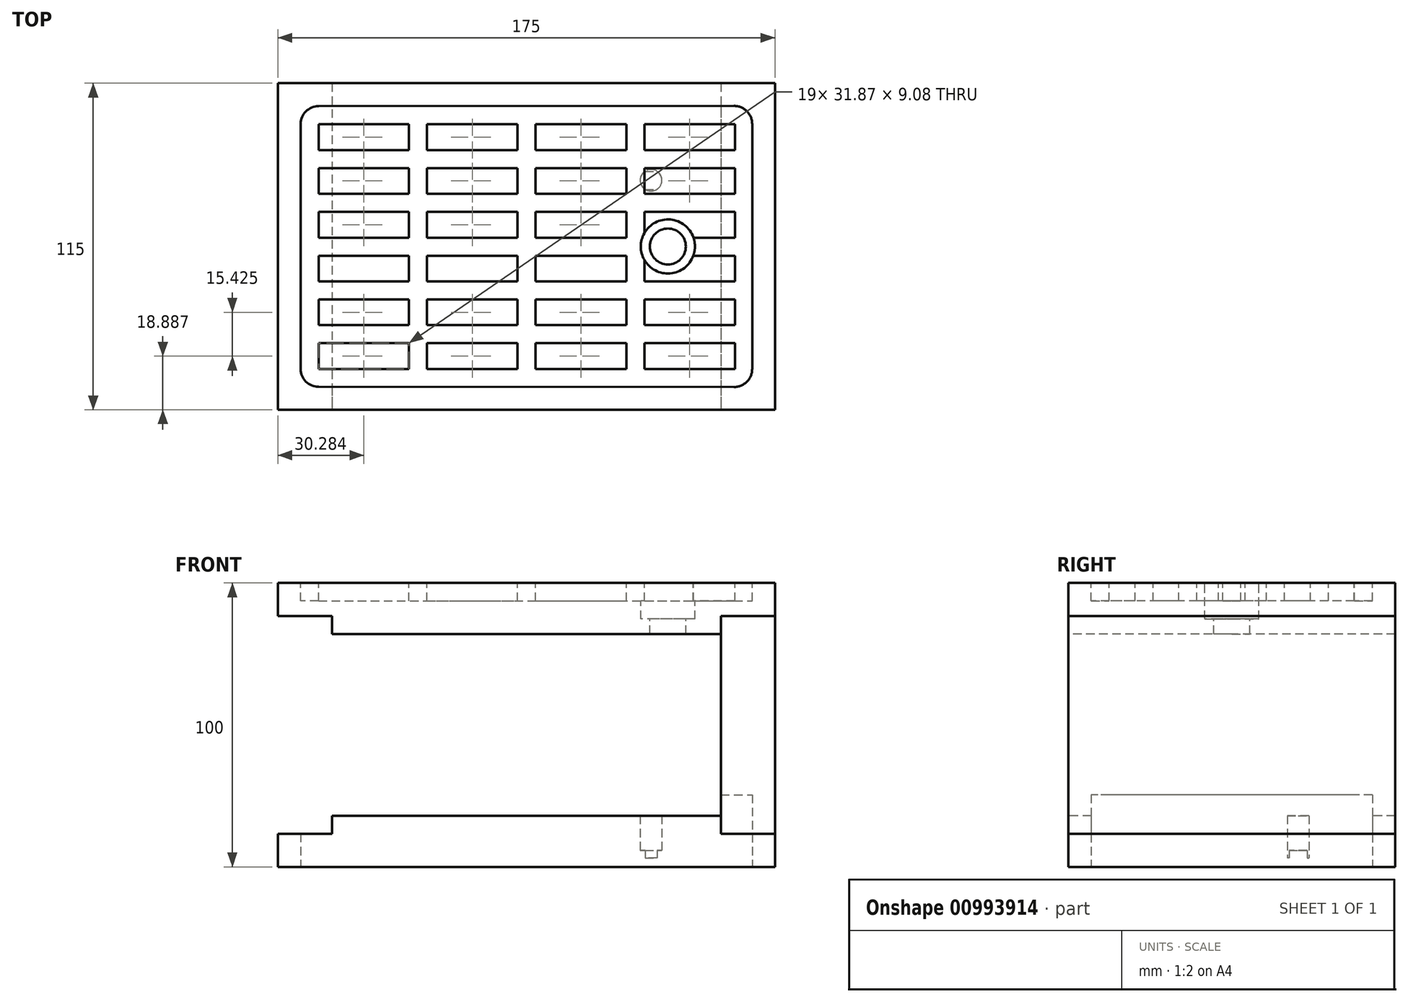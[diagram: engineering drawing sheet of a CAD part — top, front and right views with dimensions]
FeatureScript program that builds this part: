
annotation { "Feature Type Name" : "Feature", "Feature Type Description" : "" }
export const myFeature = defineFeature(function(context is Context, id is Id, definition is map)
    precondition{}
    {
        {
            var Q0;
            Q0=qCreatedBy(makeId("Front.planeOp"),FACE);
            var sketch = newSketch(context, id + "F0", { "sketchPlane" : qUnion([Q0])});
            skLineSegment(sketch, "E0.bottom", {"start": v(-125.12, 38.1) * mm, "end": v(49.88, 38.1) * mm});
            skLineSegment(sketch, "E0.top", {"start": v(-106.07, 20.1) * mm, "end": v(30.83, 20.1) * mm});
            skLineSegment(sketch, "E0.left", {"start": v(-125.12, 38.1) * mm, "end": v(-125.12, 26.44) * mm});
            skLineSegment(sketch, "E0.right", {"start": v(49.88, 38.1) * mm, "end": v(49.88, 26.44) * mm});
            skLineSegment(sketch, "E1", {"start": v(-37.62, 50.38) * mm, "end": v(-37.62, -79.55) * mm, "construction": true});
            skPoint(sketch, "E1.startSnap0", {"position": v(-37.62, 38.1) * mm});
            skLineSegment(sketch, "E2.bottom", {"start": v(-106.07, 26.44) * mm, "end": v(-125.12, 26.44) * mm});
            skLineSegment(sketch, "E2.left", {"start": v(-106.07, 26.44) * mm, "end": v(-106.07, 20.1) * mm});
            skLineSegment(sketch, "E3.MirrorCS", {"start": v(30.83, 26.44) * mm, "end": v(49.88, 26.44) * mm});
            skLineSegment(sketch, "E4.MirrorCS", {"start": v(30.83, 20.1) * mm, "end": v(30.83, 26.44) * mm});
            skLineSegment(sketch, "E5", {"start": v(-152.81, -11.9) * mm, "end": v(116.81, -11.9) * mm, "construction": true});
            skLineSegment(sketch, "E6.MirrorCS", {"start": v(-125.12, -61.9) * mm, "end": v(49.88, -61.9) * mm});
            skLineSegment(sketch, "E7.MirrorCS", {"start": v(-106.07, -43.9) * mm, "end": v(30.83, -43.9) * mm});
            skLineSegment(sketch, "E8.MirrorCS", {"start": v(-106.07, -50.26) * mm, "end": v(-125.12, -50.26) * mm});
            skLineSegment(sketch, "E9.MirrorCS", {"start": v(-106.07, -43.9) * mm, "end": v(-106.07, -50.26) * mm});
            skLineSegment(sketch, "E10.MirrorCS", {"start": v(30.83, -43.9) * mm, "end": v(30.83, -50.26) * mm});
            skLineSegment(sketch, "E11.MirrorCS", {"start": v(30.83, -50.26) * mm, "end": v(49.88, -50.26) * mm});
            skLineSegment(sketch, "E12.MirrorCS", {"start": v(49.88, -61.9) * mm, "end": v(49.88, -50.26) * mm});
            skLineSegment(sketch, "E13", {"start": v(-125.12, -50.26) * mm, "end": v(-125.12, -61.9) * mm});
            skLineSegment(sketch, "E14.left", {"start": v(-106.07, 26.44) * mm, "end": v(-106.07, -50.26) * mm, "construction": true});
            skLineSegment(sketch, "E14.right", {"start": v(-125.12, 26.44) * mm, "end": v(-125.12, -50.26) * mm, "construction": true});
            skLineSegment(sketch, "E15.MirrorCS", {"start": v(49.88, 26.44) * mm, "end": v(49.88, -50.26) * mm, "construction": true});
            skLineSegment(sketch, "E16.MirrorCS", {"start": v(30.83, 26.44) * mm, "end": v(30.83, -50.26) * mm, "construction": true});
            skLineSegment(sketch, "E17.left", {"start": v(30.83, 26.44) * mm, "end": v(30.83, -50.26) * mm});
            skLineSegment(sketch, "E17.right", {"start": v(49.88, 26.44) * mm, "end": v(49.88, -50.26) * mm});
            skSolve(sketch);
        }
        {
            var Q0;
            Q0=makeQuery(id+"F0.imprint","IMPRINT",FACE,{"disambiguationData":[TD([[makeQuery(id+"F0.imprint","IMPRINT",EDGE,{"derivedFrom":sQuery(id+"F0.wireOp",EDGE,"E0.bottom")}),-1.0]])]});
            var Q1;
            Q1=makeQuery(id+"F0.imprint","IMPRINT",FACE,{"disambiguationData":[TD([[makeQuery(id+"F0.imprint","IMPRINT",EDGE,{"derivedFrom":sQuery(id+"F0.wireOp",EDGE,"E6.MirrorCS")}),1.0]])]});
            extrude(context, id + "F1", {"entities" : qUnion([Q0, Q1]), "oppositeDirection" : true, "depth" : 115 * mm, "offsetDistance" : 25.4 * mm});
        }
        {
            var Q0;
            Q0 = qSketchRegion(id + "F0", true);
            extrude(context, id + "F2", {"entities" : qUnion([Q0]), "oppositeDirection" : true, "depth" : 115 * mm, "offsetDistance" : 25.4 * mm});
        }
        {
            var Q0;
            Q0=makeQuery(id+"F1.opExtrude","SWEPT_FACE",FACE,{"disambiguationData":[OSD([sQuery(id+"F0.wireOp",EDGE,"E0.bottom")])]});
            var sketch = newSketch(context, id + "F3", { "sketchPlane" : qUnion([Q0])});
            skLineSegment(sketch, "E18", {"start": v(64.2, 57.5) * mm, "end": v(21.17, 57.5) * mm, "construction": true});
            skPoint(sketch, "E18.startSnap0", {"position": v(49.88, 57.5) * mm});
            skPoint(sketch, "E19.startSnap0", {"position": v(-37.62, 115) * mm});
            skLineSegment(sketch, "E20.0", {"start": v(-110.77, 100.55) * mm, "end": v(-78.9, 100.55) * mm});
            skLineSegment(sketch, "E21.0", {"start": v(-110.77, 100.55) * mm, "end": v(-110.77, 91.47) * mm});
            skLineSegment(sketch, "E22.trimOffspring", {"start": v(-110.77, 14.35) * mm, "end": v(-78.9, 14.35) * mm});
            skArc(sketch, "E23", {"start": v(-110.78, 106.9) * mm, "mid": v(-115.23, 105.07) * mm, "end": v(-117.12, 100.65) * mm});
            skArc(sketch, "E24.MirrorCS", {"start": v(35.52, 107) * mm, "mid": v(40.02, 105.14) * mm, "end": v(41.88, 100.65) * mm});
            skArc(sketch, "E25.MirrorCS", {"start": v(-110.78, 8.1) * mm, "mid": v(-115.23, 9.93) * mm, "end": v(-117.12, 14.35) * mm});
            skArc(sketch, "E26.MirrorCS", {"start": v(35.52, 8) * mm, "mid": v(40.02, 9.86) * mm, "end": v(41.88, 14.35) * mm});
            skLineSegment(sketch, "E27.0", {"start": v(-110.77, 91.47) * mm, "end": v(-78.9, 91.47) * mm});
            skLineSegment(sketch, "E28.0", {"start": v(-110.77, 85.12) * mm, "end": v(-78.9, 85.12) * mm});
            skLineSegment(sketch, "E29.0", {"start": v(-110.77, 76.05) * mm, "end": v(-78.9, 76.05) * mm});
            skLineSegment(sketch, "E30.0", {"start": v(-110.77, 69.7) * mm, "end": v(-78.9, 69.7) * mm});
            skLineSegment(sketch, "E31.0", {"start": v(-110.77, 60.63) * mm, "end": v(-78.9, 60.63) * mm});
            skLineSegment(sketch, "E32.0", {"start": v(-110.77, 54.28) * mm, "end": v(3.25, 54.28) * mm});
            skLineSegment(sketch, "E33.0", {"start": v(-110.77, 45.2) * mm, "end": v(-78.9, 45.2) * mm});
            skLineSegment(sketch, "E34.0", {"start": v(-110.77, 38.85) * mm, "end": v(-78.9, 38.85) * mm});
            skLineSegment(sketch, "E35.0", {"start": v(-110.77, 29.78) * mm, "end": v(-78.9, 29.78) * mm});
            skLineSegment(sketch, "E36.0", {"start": v(-110.77, 23.43) * mm, "end": v(-78.9, 23.43) * mm});
            skLineSegment(sketch, "E37.trimOffspring", {"start": v(-110.77, 85.12) * mm, "end": v(-110.77, 76.05) * mm});
            skLineSegment(sketch, "E38.trimOffspring", {"start": v(-110.77, 69.7) * mm, "end": v(-110.77, 60.63) * mm});
            skLineSegment(sketch, "E39.trimOffspring", {"start": v(-110.77, 54.28) * mm, "end": v(-110.77, 45.2) * mm});
            skLineSegment(sketch, "E40.trimOffspring", {"start": v(-110.77, 38.85) * mm, "end": v(-110.77, 29.78) * mm});
            skLineSegment(sketch, "E41.trimOffspring", {"start": v(-110.77, 23.43) * mm, "end": v(-110.77, 14.35) * mm});
            skLineSegment(sketch, "E42.0", {"start": v(-78.9, 100.55) * mm, "end": v(-78.9, 91.47) * mm});
            skLineSegment(sketch, "E43.0", {"start": v(-131.47, -6.35) * mm, "end": v(56.23, -6.35) * mm});
            skLineSegment(sketch, "E43.1", {"start": v(-131.47, 121.35) * mm, "end": v(-131.47, -6.35) * mm});
            skLineSegment(sketch, "E43.2", {"start": v(56.23, 121.35) * mm, "end": v(-131.47, 121.35) * mm});
            skLineSegment(sketch, "E43.3", {"start": v(56.23, -6.35) * mm, "end": v(56.23, 121.35) * mm});
            skLineSegment(sketch, "E44.trimOffspring", {"start": v(-78.9, 57.5) * mm, "end": v(-137, 57.5) * mm, "construction": true});
            skLineSegment(sketch, "E45.trimOffspring", {"start": v(-78.9, 23.43) * mm, "end": v(-78.9, 14.35) * mm});
            skLineSegment(sketch, "E46.trimOffspring", {"start": v(-78.9, 38.85) * mm, "end": v(-78.9, 29.78) * mm});
            skLineSegment(sketch, "E47.trimOffspring", {"start": v(-78.9, 54.28) * mm, "end": v(-78.9, 45.2) * mm});
            skLineSegment(sketch, "E48.trimOffspring", {"start": v(-78.9, 69.7) * mm, "end": v(-78.9, 60.63) * mm});
            skLineSegment(sketch, "E49.trimOffspring", {"start": v(-78.9, 85.12) * mm, "end": v(-78.9, 76.05) * mm});
            skLineSegment(sketch, "E50.MirrorCS", {"start": v(41.88, 100.65) * mm, "end": v(41.88, 14.25) * mm});
            skArc(sketch, "E51.MirrorCS", {"start": v(35.52, 8) * mm, "mid": v(39.98, 9.82) * mm, "end": v(41.88, 14.25) * mm});
            skLineSegment(sketch, "E52.bottom", {"start": v(-110.77, 54.28) * mm, "end": v(-78.9, 54.28) * mm});
            skCircle(sketch, "E53", {"center": v(12.2, 57.5) * mm, "radius": 6.32 * mm});
            skLineSegment(sketch, "E54", {"start": v(-94.84, 100.55) * mm, "end": v(-94.84, 91.47) * mm, "construction": true});
            skLineSegment(sketch, "E55", {"start": v(-94.84, 91.47) * mm, "end": v(-94.5, 90.59) * mm, "construction": true});
            skLineSegment(sketch, "E56", {"start": v(-94.84, 85.12) * mm, "end": v(-94.84, 76.05) * mm, "construction": true});
            skLineSegment(sketch, "E57", {"start": v(-94.84, 76.05) * mm, "end": v(-94.14, 76.72) * mm, "construction": true});
            skLineSegment(sketch, "E58", {"start": v(-94.84, 69.7) * mm, "end": v(-94.84, 60.63) * mm, "construction": true});
            skLineSegment(sketch, "E59", {"start": v(-94.84, 60.63) * mm, "end": v(-94.12, 61.09) * mm, "construction": true});
            skLineSegment(sketch, "E60", {"start": v(-94.84, 54.28) * mm, "end": v(-94.84, 45.2) * mm, "construction": true});
            skLineSegment(sketch, "E61", {"start": v(-94.84, 38.85) * mm, "end": v(-94.84, 29.78) * mm, "construction": true});
            skLineSegment(sketch, "E62", {"start": v(-94.84, 29.78) * mm, "end": v(-94.77, 30.91) * mm, "construction": true});
            skLineSegment(sketch, "E63", {"start": v(-94.84, 23.43) * mm, "end": v(-94.84, 14.35) * mm, "construction": true});
            skLineSegment(sketch, "E64", {"start": v(-94.84, 14.35) * mm, "end": v(-95.42, 15.1) * mm, "construction": true});
            skLineSegment(sketch, "E65.1.0.0", {"start": v(-40.67, 23.43) * mm, "end": v(-40.67, 14.35) * mm});
            skLineSegment(sketch, "E65.1.0.1", {"start": v(-40.67, 69.7) * mm, "end": v(-40.67, 60.63) * mm});
            skLineSegment(sketch, "E65.1.0.2", {"start": v(-72.54, 60.63) * mm, "end": v(-40.67, 60.63) * mm});
            skLineSegment(sketch, "E65.1.0.3", {"start": v(-40.67, 54.28) * mm, "end": v(-40.67, 45.2) * mm});
            skLineSegment(sketch, "E65.1.0.4", {"start": v(-72.54, 29.78) * mm, "end": v(-40.67, 29.78) * mm});
            skLineSegment(sketch, "E65.1.0.5", {"start": v(-72.54, 76.05) * mm, "end": v(-40.67, 76.05) * mm});
            skLineSegment(sketch, "E65.1.0.6", {"start": v(-56.6, 100.55) * mm, "end": v(-56.6, 91.47) * mm, "construction": true});
            skLineSegment(sketch, "E65.1.0.7", {"start": v(-56.6, 85.12) * mm, "end": v(-56.6, 76.05) * mm, "construction": true});
            skLineSegment(sketch, "E65.1.0.9", {"start": v(-72.54, 23.43) * mm, "end": v(-72.54, 14.35) * mm});
            skLineSegment(sketch, "E65.1.0.10", {"start": v(-72.54, 69.7) * mm, "end": v(-72.54, 60.63) * mm});
            skLineSegment(sketch, "E65.1.0.11", {"start": v(-40.67, 85.12) * mm, "end": v(-40.67, 76.05) * mm});
            skLineSegment(sketch, "E65.1.0.12", {"start": v(-56.6, 54.28) * mm, "end": v(-56.6, 45.2) * mm, "construction": true});
            skLineSegment(sketch, "E65.1.0.13", {"start": v(-72.54, 85.12) * mm, "end": v(-72.54, 76.05) * mm});
            skLineSegment(sketch, "E65.1.0.14", {"start": v(-56.6, 69.7) * mm, "end": v(-56.6, 60.63) * mm, "construction": true});
            skLineSegment(sketch, "E65.1.0.15", {"start": v(-40.67, 100.55) * mm, "end": v(-40.67, 91.47) * mm});
            skLineSegment(sketch, "E65.1.0.16", {"start": v(-72.54, 23.43) * mm, "end": v(-40.67, 23.43) * mm});
            skLineSegment(sketch, "E65.1.0.17", {"start": v(-56.6, 38.85) * mm, "end": v(-56.6, 29.78) * mm, "construction": true});
            skLineSegment(sketch, "E65.1.0.18", {"start": v(-72.54, 69.7) * mm, "end": v(-40.67, 69.7) * mm});
            skLineSegment(sketch, "E65.1.0.19", {"start": v(-72.54, 38.85) * mm, "end": v(-40.67, 38.85) * mm});
            skLineSegment(sketch, "E65.1.0.20", {"start": v(-40.67, 38.85) * mm, "end": v(-40.67, 29.78) * mm});
            skLineSegment(sketch, "E65.1.0.21", {"start": v(-72.54, 100.55) * mm, "end": v(-40.67, 100.55) * mm});
            skLineSegment(sketch, "E65.1.0.22", {"start": v(-72.54, 54.28) * mm, "end": v(-40.67, 54.28) * mm});
            skLineSegment(sketch, "E65.1.0.23", {"start": v(-72.54, 85.12) * mm, "end": v(-40.67, 85.12) * mm});
            skLineSegment(sketch, "E65.1.0.24", {"start": v(-72.54, 45.2) * mm, "end": v(-40.67, 45.2) * mm});
            skLineSegment(sketch, "E65.1.0.25", {"start": v(-72.54, 38.85) * mm, "end": v(-72.54, 29.78) * mm});
            skLineSegment(sketch, "E65.1.0.26", {"start": v(-56.6, 23.43) * mm, "end": v(-56.6, 14.35) * mm, "construction": true});
            skLineSegment(sketch, "E65.1.0.27", {"start": v(-72.54, 14.35) * mm, "end": v(-40.67, 14.35) * mm});
            skLineSegment(sketch, "E65.1.0.28", {"start": v(-72.54, 91.47) * mm, "end": v(-40.67, 91.47) * mm});
            skLineSegment(sketch, "E65.1.0.29", {"start": v(-72.54, 100.55) * mm, "end": v(-72.54, 91.47) * mm});
            skLineSegment(sketch, "E65.1.0.30", {"start": v(-72.54, 54.28) * mm, "end": v(-72.54, 45.2) * mm});
            skLineSegment(sketch, "E65.1.0.31", {"start": v(-72.54, 54.28) * mm, "end": v(-72.54, 45.2) * mm});
            skLineSegment(sketch, "E65.1.0.32", {"start": v(-40.67, 54.28) * mm, "end": v(-40.67, 45.2) * mm});
            skLineSegment(sketch, "E65.1.0.33", {"start": v(-40.67, 100.55) * mm, "end": v(-40.67, 91.47) * mm});
            skLineSegment(sketch, "E65.1.0.34", {"start": v(-72.54, 45.2) * mm, "end": v(-40.67, 45.2) * mm});
            skLineSegment(sketch, "E65.1.0.35", {"start": v(-56.6, 29.78) * mm, "end": v(-56.54, 30.91) * mm, "construction": true});
            skLineSegment(sketch, "E65.1.0.36", {"start": v(-56.6, 14.35) * mm, "end": v(-57.2, 15.1) * mm, "construction": true});
            skLineSegment(sketch, "E65.1.0.37", {"start": v(-56.6, 91.47) * mm, "end": v(-56.27, 90.59) * mm, "construction": true});
            skLineSegment(sketch, "E65.1.0.38", {"start": v(-56.6, 76.05) * mm, "end": v(-55.9, 76.72) * mm, "construction": true});
            skLineSegment(sketch, "E65.1.0.39", {"start": v(-56.6, 60.63) * mm, "end": v(-55.89, 61.09) * mm, "construction": true});
            skLineSegment(sketch, "E65.2.0.0", {"start": v(-2.45, 23.43) * mm, "end": v(-2.45, 14.35) * mm});
            skLineSegment(sketch, "E65.2.0.1", {"start": v(-2.45, 69.7) * mm, "end": v(-2.45, 60.63) * mm});
            skLineSegment(sketch, "E65.2.0.2", {"start": v(-34.32, 60.63) * mm, "end": v(-2.45, 60.63) * mm});
            skLineSegment(sketch, "E65.2.0.3", {"start": v(-2.45, 54.28) * mm, "end": v(-2.45, 45.2) * mm});
            skLineSegment(sketch, "E65.2.0.4", {"start": v(-34.32, 29.78) * mm, "end": v(-2.45, 29.78) * mm});
            skLineSegment(sketch, "E65.2.0.5", {"start": v(-34.32, 76.05) * mm, "end": v(-2.45, 76.05) * mm});
            skLineSegment(sketch, "E65.2.0.6", {"start": v(-18.38, 100.55) * mm, "end": v(-18.38, 91.47) * mm, "construction": true});
            skLineSegment(sketch, "E65.2.0.7", {"start": v(-18.38, 85.12) * mm, "end": v(-18.38, 76.05) * mm, "construction": true});
            skLineSegment(sketch, "E65.2.0.9", {"start": v(-34.32, 23.43) * mm, "end": v(-34.32, 14.35) * mm});
            skLineSegment(sketch, "E65.2.0.10", {"start": v(-34.32, 69.7) * mm, "end": v(-34.32, 60.63) * mm});
            skLineSegment(sketch, "E65.2.0.11", {"start": v(-2.45, 85.12) * mm, "end": v(-2.45, 76.05) * mm});
            skLineSegment(sketch, "E65.2.0.12", {"start": v(-18.38, 54.28) * mm, "end": v(-18.38, 45.2) * mm, "construction": true});
            skLineSegment(sketch, "E65.2.0.13", {"start": v(-34.32, 85.12) * mm, "end": v(-34.32, 76.05) * mm});
            skLineSegment(sketch, "E65.2.0.14", {"start": v(-18.38, 69.7) * mm, "end": v(-18.38, 60.63) * mm, "construction": true});
            skLineSegment(sketch, "E65.2.0.15", {"start": v(-2.45, 100.55) * mm, "end": v(-2.45, 91.47) * mm});
            skLineSegment(sketch, "E65.2.0.16", {"start": v(-34.32, 23.43) * mm, "end": v(-2.45, 23.43) * mm});
            skLineSegment(sketch, "E65.2.0.17", {"start": v(-18.38, 38.85) * mm, "end": v(-18.38, 29.78) * mm, "construction": true});
            skLineSegment(sketch, "E65.2.0.18", {"start": v(-34.32, 69.7) * mm, "end": v(-2.45, 69.7) * mm});
            skLineSegment(sketch, "E65.2.0.19", {"start": v(-34.32, 38.85) * mm, "end": v(-2.45, 38.85) * mm});
            skLineSegment(sketch, "E65.2.0.20", {"start": v(-2.45, 38.85) * mm, "end": v(-2.45, 29.78) * mm});
            skLineSegment(sketch, "E65.2.0.21", {"start": v(-34.32, 100.55) * mm, "end": v(-2.45, 100.55) * mm});
            skLineSegment(sketch, "E65.2.0.22", {"start": v(-34.32, 54.28) * mm, "end": v(-2.45, 54.28) * mm});
            skLineSegment(sketch, "E65.2.0.23", {"start": v(-34.32, 85.12) * mm, "end": v(-2.45, 85.12) * mm});
            skLineSegment(sketch, "E65.2.0.24", {"start": v(-34.32, 45.2) * mm, "end": v(-2.45, 45.2) * mm});
            skLineSegment(sketch, "E65.2.0.25", {"start": v(-34.32, 38.85) * mm, "end": v(-34.32, 29.78) * mm});
            skLineSegment(sketch, "E65.2.0.26", {"start": v(-18.38, 23.43) * mm, "end": v(-18.38, 14.35) * mm, "construction": true});
            skLineSegment(sketch, "E65.2.0.27", {"start": v(-34.32, 14.35) * mm, "end": v(-2.45, 14.35) * mm});
            skLineSegment(sketch, "E65.2.0.28", {"start": v(-34.32, 91.47) * mm, "end": v(-2.45, 91.47) * mm});
            skLineSegment(sketch, "E65.2.0.29", {"start": v(-34.32, 100.55) * mm, "end": v(-34.32, 91.47) * mm});
            skLineSegment(sketch, "E65.2.0.30", {"start": v(-34.32, 54.28) * mm, "end": v(-34.32, 45.2) * mm});
            skLineSegment(sketch, "E65.2.0.31", {"start": v(-34.32, 54.28) * mm, "end": v(-34.32, 45.2) * mm});
            skLineSegment(sketch, "E65.2.0.32", {"start": v(-2.45, 54.28) * mm, "end": v(-2.45, 45.2) * mm});
            skLineSegment(sketch, "E65.2.0.33", {"start": v(-2.45, 100.55) * mm, "end": v(-2.45, 91.47) * mm});
            skLineSegment(sketch, "E65.2.0.34", {"start": v(-34.32, 45.2) * mm, "end": v(-2.45, 45.2) * mm});
            skLineSegment(sketch, "E65.2.0.35", {"start": v(-18.38, 29.78) * mm, "end": v(-18.31, 30.91) * mm, "construction": true});
            skLineSegment(sketch, "E65.2.0.36", {"start": v(-18.38, 14.35) * mm, "end": v(-18.97, 15.1) * mm, "construction": true});
            skLineSegment(sketch, "E65.2.0.37", {"start": v(-18.38, 91.47) * mm, "end": v(-18.04, 90.59) * mm, "construction": true});
            skLineSegment(sketch, "E65.2.0.38", {"start": v(-18.38, 76.05) * mm, "end": v(-17.68, 76.72) * mm, "construction": true});
            skLineSegment(sketch, "E65.2.0.39", {"start": v(-18.38, 60.63) * mm, "end": v(-17.66, 61.09) * mm, "construction": true});
            skLineSegment(sketch, "E65.3.0.0", {"start": v(35.78, 23.43) * mm, "end": v(35.78, 14.35) * mm});
            skLineSegment(sketch, "E65.3.0.1", {"start": v(35.78, 69.7) * mm, "end": v(35.78, 60.63) * mm});
            skLineSegment(sketch, "E65.3.0.3", {"start": v(35.78, 54.28) * mm, "end": v(35.78, 45.2) * mm});
            skLineSegment(sketch, "E65.3.0.4", {"start": v(3.9, 29.78) * mm, "end": v(35.78, 29.78) * mm});
            skLineSegment(sketch, "E65.3.0.5", {"start": v(3.9, 76.05) * mm, "end": v(35.78, 76.05) * mm});
            skLineSegment(sketch, "E65.3.0.6", {"start": v(19.85, 100.55) * mm, "end": v(19.85, 91.47) * mm, "construction": true});
            skLineSegment(sketch, "E65.3.0.7", {"start": v(19.85, 85.12) * mm, "end": v(19.85, 76.05) * mm, "construction": true});
            skLineSegment(sketch, "E65.3.0.9", {"start": v(3.9, 23.43) * mm, "end": v(3.9, 14.35) * mm});
            skLineSegment(sketch, "E65.3.0.10", {"start": v(3.9, 69.7) * mm, "end": v(3.9, 62.17) * mm});
            skLineSegment(sketch, "E65.3.0.11", {"start": v(35.78, 85.12) * mm, "end": v(35.78, 76.05) * mm});
            skLineSegment(sketch, "E65.3.0.12", {"start": v(19.85, 54.28) * mm, "end": v(19.85, 45.2) * mm, "construction": true});
            skLineSegment(sketch, "E65.3.0.13", {"start": v(3.9, 85.12) * mm, "end": v(3.9, 76.05) * mm});
            skLineSegment(sketch, "E65.3.0.14", {"start": v(19.85, 69.7) * mm, "end": v(19.85, 60.63) * mm, "construction": true});
            skLineSegment(sketch, "E65.3.0.15", {"start": v(35.78, 100.55) * mm, "end": v(35.78, 91.47) * mm});
            skLineSegment(sketch, "E65.3.0.16", {"start": v(3.9, 23.43) * mm, "end": v(35.78, 23.43) * mm});
            skLineSegment(sketch, "E65.3.0.17", {"start": v(19.85, 38.85) * mm, "end": v(19.85, 29.78) * mm, "construction": true});
            skLineSegment(sketch, "E65.3.0.18", {"start": v(3.9, 69.7) * mm, "end": v(35.78, 69.7) * mm});
            skLineSegment(sketch, "E65.3.0.19", {"start": v(3.9, 38.85) * mm, "end": v(35.78, 38.85) * mm});
            skLineSegment(sketch, "E65.3.0.20", {"start": v(35.78, 38.85) * mm, "end": v(35.78, 29.78) * mm});
            skLineSegment(sketch, "E65.3.0.21", {"start": v(3.9, 100.55) * mm, "end": v(35.78, 100.55) * mm});
            skLineSegment(sketch, "E65.3.0.23", {"start": v(3.9, 85.12) * mm, "end": v(35.78, 85.12) * mm});
            skLineSegment(sketch, "E65.3.0.24", {"start": v(3.9, 45.2) * mm, "end": v(35.78, 45.2) * mm});
            skLineSegment(sketch, "E65.3.0.25", {"start": v(3.9, 38.85) * mm, "end": v(3.9, 29.78) * mm});
            skLineSegment(sketch, "E65.3.0.26", {"start": v(19.85, 23.43) * mm, "end": v(19.85, 14.35) * mm, "construction": true});
            skLineSegment(sketch, "E65.3.0.27", {"start": v(3.9, 14.35) * mm, "end": v(35.78, 14.35) * mm});
            skLineSegment(sketch, "E65.3.0.28", {"start": v(3.9, 91.47) * mm, "end": v(35.78, 91.47) * mm});
            skLineSegment(sketch, "E65.3.0.29", {"start": v(3.9, 100.55) * mm, "end": v(3.9, 91.47) * mm});
            skLineSegment(sketch, "E65.3.0.30", {"start": v(3.9, 52.83) * mm, "end": v(3.9, 45.2) * mm});
            skLineSegment(sketch, "E65.3.0.31", {"start": v(3.9, 49.6) * mm, "end": v(3.9, 45.2) * mm});
            skLineSegment(sketch, "E65.3.0.32", {"start": v(35.78, 54.28) * mm, "end": v(35.78, 45.2) * mm});
            skLineSegment(sketch, "E65.3.0.33", {"start": v(35.78, 100.55) * mm, "end": v(35.78, 91.47) * mm});
            skLineSegment(sketch, "E65.3.0.34", {"start": v(3.9, 45.2) * mm, "end": v(35.78, 45.2) * mm});
            skLineSegment(sketch, "E65.3.0.35", {"start": v(19.85, 29.78) * mm, "end": v(19.92, 30.91) * mm, "construction": true});
            skLineSegment(sketch, "E65.3.0.36", {"start": v(19.85, 14.35) * mm, "end": v(19.26, 15.1) * mm, "construction": true});
            skLineSegment(sketch, "E65.3.0.37", {"start": v(19.85, 91.47) * mm, "end": v(20.18, 90.59) * mm, "construction": true});
            skLineSegment(sketch, "E65.3.0.38", {"start": v(19.85, 76.05) * mm, "end": v(20.55, 76.72) * mm, "construction": true});
            skLineSegment(sketch, "E65.3.0.39", {"start": v(19.85, 60.63) * mm, "end": v(20.56, 61.09) * mm, "construction": true});
            skLineSegment(sketch, "E65.direction1", {"start": v(-110.77, 14.35) * mm, "end": v(-72.54, 14.35) * mm, "construction": true});
            skPoint(sketch, "E66.orphan", {"position": v(3.9, 54.28) * mm});
            skLineSegment(sketch, "E67", {"start": v(-110.78, 106.9) * mm, "end": v(35.52, 107) * mm});
            skLineSegment(sketch, "E68", {"start": v(-117.12, 100.65) * mm, "end": v(-117.12, 14.35) * mm});
            skLineSegment(sketch, "E69", {"start": v(-110.78, 8.1) * mm, "end": v(35.52, 8) * mm});
            skPoint(sketch, "E70.orphan", {"position": v(-78.9, 20.9) * mm});
            skPoint(sketch, "E71.orphan", {"position": v(-72.54, 20.9) * mm});
            skPoint(sketch, "E72.orphan", {"position": v(-34.32, 20.9) * mm});
            skPoint(sketch, "E73.orphan", {"position": v(3.9, 20.9) * mm});
            skLineSegment(sketch, "E74", {"start": v(64.2, 57.5) * mm, "end": v(-137, 57.5) * mm, "construction": true});
            skLineSegment(sketch, "E75", {"start": v(12.2, 106.13) * mm, "end": v(12.2, 57.5) * mm, "construction": true});
            skLineSegment(sketch, "E76", {"start": v(35.78, 60.63) * mm, "end": v(21.2, 60.63) * mm});
            skLineSegment(sketch, "E77", {"start": v(21.17, 54.28) * mm, "end": v(35.78, 54.28) * mm});
            skCircle(sketch, "E78", {"center": v(12.2, 57.5) * mm, "radius": 9.53 * mm});
            skPoint(sketch, "E79.orphan", {"position": v(3.9, 60.63) * mm});
            skSolve(sketch);
        }
        {
            var Q0;
            Q0=makeQuery(id+"F3.imprint","IMPRINT",FACE,{"disambiguationData":[TD([[makeQuery(id+"F3.imprint","IMPRINT",EDGE,{"derivedFrom":sQuery(id+"F3.wireOp",EDGE,"E20.0")}),1.0]])]});
            var Q1;
            Q1=makeQuery(id+"F1.opExtrude","SWEPT_FACE",FACE,{"disambiguationData":[OSD([sQuery(id+"F0.wireOp",EDGE,"E0.bottom")])]});
            extrude(context, id + "F4", {"entities" : qUnion([Q0]), "operationType" : NewBodyOperationType.REMOVE, "oppositeDirection" : true, "depth" : 6.35 * mm, "offsetDistance" : 25.4 * mm});
        }
        {
            var Q0;
            Q0=makeQuery(id+"F1.opExtrude","SWEPT_FACE",FACE,{"disambiguationData":[OSD([sQuery(id+"F0.wireOp",EDGE,"E6.MirrorCS")])]});
            var sketch = newSketch(context, id + "F5", { "sketchPlane" : qUnion([Q0])});
            skLineSegment(sketch, "E80", {"start": v(63.73, -57.5) * mm, "end": v(-168.08, -57.5) * mm, "construction": true});
            skPoint(sketch, "E80.startSnap0", {"position": v(49.88, -57.5) * mm});
            skLineSegment(sketch, "E81", {"start": v(-37.62, 14.21) * mm, "end": v(-37.62, -124.17) * mm, "construction": true});
            skPoint(sketch, "E81.startSnap0", {"position": v(-37.62, 0) * mm});
            skPoint(sketch, "E81.endSnap0", {"position": v(-37.62, -115) * mm});
            skLineSegment(sketch, "E82.0", {"start": v(41.88, -100.65) * mm, "end": v(41.88, -14.35) * mm});
            skLineSegment(sketch, "E83.0", {"start": v(-110.77, -8) * mm, "end": v(35.53, -8) * mm});
            skArc(sketch, "E84.trimOffspring", {"start": v(41.88, -14.35) * mm, "mid": v(40.02, -9.86) * mm, "end": v(35.53, -8) * mm});
            skArc(sketch, "E85.MirrorCS", {"start": v(-117.12, -14.35) * mm, "mid": v(-115.26, -9.86) * mm, "end": v(-110.77, -8) * mm});
            skLineSegment(sketch, "E86.MirrorCS", {"start": v(-110.77, -100.65) * mm, "end": v(-110.77, -14.35) * mm});
            skArc(sketch, "E87.MirrorCS", {"start": v(-117.12, -100.65) * mm, "mid": v(-115.26, -105.14) * mm, "end": v(-110.77, -107) * mm});
            skArc(sketch, "E88.MirrorCS", {"start": v(41.88, -100.65) * mm, "mid": v(40.02, -105.14) * mm, "end": v(35.53, -107) * mm});
            skLineSegment(sketch, "E89.MirrorCS", {"start": v(-110.77, -107) * mm, "end": v(35.53, -107) * mm});
            skLineSegment(sketch, "E90.trimOffspring", {"start": v(-110.77, -14.35) * mm, "end": v(35.53, -14.35) * mm});
            skPoint(sketch, "E91.0.start.orphan", {"position": v(-125.12, -14.35) * mm});
            skPoint(sketch, "E92.orphan", {"position": v(-125.12, -8) * mm});
            skLineSegment(sketch, "E93.trimOffspring", {"start": v(35.53, -100.65) * mm, "end": v(35.53, -14.35) * mm});
            skPoint(sketch, "E94.orphan", {"position": v(41.88, -115) * mm});
            skPoint(sketch, "E95.0.start.orphan", {"position": v(35.53, -115) * mm});
            skLineSegment(sketch, "E96.trimOffspring", {"start": v(-117.12, -100.65) * mm, "end": v(-117.12, -14.35) * mm});
            skPoint(sketch, "E97.MirrorCS.start.orphan", {"position": v(-117.12, -115) * mm});
            skPoint(sketch, "E98.orphan", {"position": v(-125.12, -107) * mm});
            skPoint(sketch, "E99.orphan", {"position": v(-110.77, -115) * mm});
            skLineSegment(sketch, "E100.trimOffspring", {"start": v(-110.77, -100.65) * mm, "end": v(35.53, -100.65) * mm});
            skPoint(sketch, "E101.MirrorCS.start.orphan", {"position": v(-125.12, -100.65) * mm});
            skLineSegment(sketch, "E102.bottom", {"start": v(-101.12, -60.68) * mm, "end": v(25.88, -60.68) * mm});
            skLineSegment(sketch, "E102.top", {"start": v(-101.12, -54.33) * mm, "end": v(25.88, -54.33) * mm});
            skLineSegment(sketch, "E102.left", {"start": v(-101.12, -60.68) * mm, "end": v(-101.12, -54.33) * mm});
            skLineSegment(sketch, "E102.right", {"start": v(25.88, -60.68) * mm, "end": v(25.88, -54.33) * mm});
            skPoint(sketch, "E102.middle", {"position": v(-37.62, -57.5) * mm});
            skLineSegment(sketch, "E103", {"start": v(-101.12, -54.33) * mm, "end": v(-101.12, -37.36) * mm, "construction": true});
            skLineSegment(sketch, "E104.MirrorCS", {"start": v(25.88, -54.33) * mm, "end": v(25.88, -37.36) * mm, "construction": true});
            skLineSegment(sketch, "E105.bottom", {"start": v(-101.12, -37.36) * mm, "end": v(25.88, -37.36) * mm});
            skLineSegment(sketch, "E105.top", {"start": v(-101.12, -31) * mm, "end": v(25.88, -31) * mm});
            skLineSegment(sketch, "E105.left", {"start": v(-101.12, -37.36) * mm, "end": v(-101.12, -31) * mm});
            skLineSegment(sketch, "E105.right", {"start": v(25.88, -37.36) * mm, "end": v(25.88, -31) * mm});
            skLineSegment(sketch, "E106.MirrorCS", {"start": v(-101.12, -77.64) * mm, "end": v(25.88, -77.64) * mm});
            skLineSegment(sketch, "E107.MirrorCS", {"start": v(-101.12, -84) * mm, "end": v(25.88, -84) * mm});
            skLineSegment(sketch, "E108.MirrorCS", {"start": v(-101.12, -77.64) * mm, "end": v(-101.12, -84) * mm});
            skLineSegment(sketch, "E109.MirrorCS", {"start": v(25.88, -77.64) * mm, "end": v(25.88, -84) * mm});
            skLineSegment(sketch, "E110.0", {"start": v(-81.51, -100.65) * mm, "end": v(-81.51, -14.35) * mm, "construction": true});
            skLineSegment(sketch, "E111.0", {"start": v(-52.25, -100.65) * mm, "end": v(-52.25, -14.35) * mm, "construction": true});
            skLineSegment(sketch, "E112.0", {"start": v(-22.99, -100.65) * mm, "end": v(-22.99, -14.35) * mm, "construction": true});
            skLineSegment(sketch, "E113.0", {"start": v(6.27, -100.65) * mm, "end": v(6.27, -14.35) * mm, "construction": true});
            skLineSegment(sketch, "E114.bottom", {"start": v(9.45, -107) * mm, "end": v(3.1, -107) * mm});
            skLineSegment(sketch, "E114.top", {"start": v(9.45, -8) * mm, "end": v(3.1, -8) * mm});
            skLineSegment(sketch, "E114.left", {"start": v(9.45, -100.65) * mm, "end": v(9.45, -14.35) * mm});
            skLineSegment(sketch, "E114.right", {"start": v(3.1, -100.65) * mm, "end": v(3.1, -14.35) * mm});
            skPoint(sketch, "E114.middle", {"position": v(6.27, -57.5) * mm});
            skLineSegment(sketch, "E115.bottom", {"start": v(-19.81, -100.65) * mm, "end": v(-26.16, -100.65) * mm});
            skLineSegment(sketch, "E115.top", {"start": v(-19.81, -14.35) * mm, "end": v(-26.16, -14.35) * mm});
            skLineSegment(sketch, "E115.left", {"start": v(-19.81, -100.65) * mm, "end": v(-19.81, -14.35) * mm});
            skLineSegment(sketch, "E115.right", {"start": v(-26.16, -100.65) * mm, "end": v(-26.16, -14.35) * mm});
            skPoint(sketch, "E115.middle", {"position": v(-22.99, -57.5) * mm});
            skLineSegment(sketch, "E116.bottom", {"start": v(-49, -100.65) * mm, "end": v(-55.35, -100.65) * mm});
            skLineSegment(sketch, "E116.top", {"start": v(-49, -14.35) * mm, "end": v(-55.35, -14.35) * mm});
            skLineSegment(sketch, "E116.left", {"start": v(-49, -100.65) * mm, "end": v(-49, -14.35) * mm});
            skLineSegment(sketch, "E116.right", {"start": v(-55.35, -100.65) * mm, "end": v(-55.35, -14.35) * mm});
            skPoint(sketch, "E116.middle", {"position": v(-52.18, -57.5) * mm});
            skLineSegment(sketch, "E117.bottom", {"start": v(-78.34, -100.65) * mm, "end": v(-84.69, -100.65) * mm});
            skLineSegment(sketch, "E117.top", {"start": v(-78.34, -14.35) * mm, "end": v(-84.69, -14.35) * mm});
            skLineSegment(sketch, "E117.left", {"start": v(-78.34, -100.65) * mm, "end": v(-78.34, -14.35) * mm});
            skLineSegment(sketch, "E117.right", {"start": v(-84.69, -100.65) * mm, "end": v(-84.69, -14.35) * mm});
            skPoint(sketch, "E117.middle", {"position": v(-81.51, -57.5) * mm});
            skSolve(sketch);
        }
        {
            var Q0;
            {var subQ0=sQuery(id+"F5.wireOp",EDGE,"E117.left");var subQ1=sQuery(id+"F5.wireOp",EDGE,"E105.bottom");var subQ2=makeQuery(id+"F5.imprint","INTERSECT",VERTEX,{"derivedFrom":[subQ1,subQ0]});var subQ10=sQuery(id+"F5.wireOp",EDGE,"E105.right");var subQ15=sQuery(id+"F5.wireOp",EDGE,"E116.left");var subQ16=makeQuery(id+"F5.imprint","INTERSECT",VERTEX,{"derivedFrom":[subQ1,subQ15]});var subQ23=sQuery(id+"F5.wireOp",EDGE,"E105.left");var subQ24=sQuery(id+"F5.wireOp",EDGE,"E115.left");var subQ25=makeQuery(id+"F5.imprint","INTERSECT",VERTEX,{"derivedFrom":[subQ1,subQ24]});var subQ32=sQuery(id+"F5.wireOp",EDGE,"E114.right");var subQ33=makeQuery(id+"F5.imprint","INTERSECT",VERTEX,{"derivedFrom":[subQ1,subQ32]});Q0=qUnion([makeQuery(id+"F5.imprint","IMPRINT",FACE,{"disambiguationData":[TD([[makeQuery(id+"F5.imprint","IMPRINT",EDGE,{"disambiguationData":[TD([[subQ25,-1.0]])],"derivedFrom":subQ1}),1.0]])]}),makeQuery(id+"F5.imprint","IMPRINT",FACE,{"disambiguationData":[TD([[makeQuery(id+"F5.imprint","IMPRINT",EDGE,{"disambiguationData":[TD([[subQ33,-1.0]])],"derivedFrom":subQ1}),1.0]])]}),makeQuery(id+"F5.imprint","IMPRINT",FACE,{"disambiguationData":[TD([[makeQuery(id+"F5.imprint","IMPRINT",EDGE,{"disambiguationData":[TD([[subQ2,-1.0]])],"derivedFrom":subQ1}),1.0]])]}),makeQuery(id+"F5.imprint","IMPRINT",FACE,{"disambiguationData":[TD([[makeQuery(id+"F5.imprint","IMPRINT",EDGE,{"disambiguationData":[TD([[subQ16,1.0]])],"derivedFrom":subQ1}),1.0]])]}),makeQuery(id+"F5.imprint","IMPRINT",FACE,{"disambiguationData":[TD([[makeQuery(id+"F5.imprint","IMPRINT",EDGE,{"disambiguationData":[TD([[subQ25,1.0]])],"derivedFrom":subQ1}),1.0]])]}),makeQuery(id+"F5.imprint","IMPRINT",FACE,{"disambiguationData":[TD([[makeQuery(id+"F5.imprint","IMPRINT",EDGE,{"derivedFrom":subQ23}),-1.0]])]}),makeQuery(id+"F5.imprint","IMPRINT",FACE,{"disambiguationData":[TD([[makeQuery(id+"F5.imprint","IMPRINT",EDGE,{"disambiguationData":[TD([[subQ16,-1.0]])],"derivedFrom":subQ1}),1.0]])]}),makeQuery(id+"F5.imprint","IMPRINT",FACE,{"disambiguationData":[TD([[makeQuery(id+"F5.imprint","IMPRINT",EDGE,{"derivedFrom":subQ10}),1.0]])]}),makeQuery(id+"F5.imprint","IMPRINT",FACE,{"disambiguationData":[TD([[makeQuery(id+"F5.imprint","IMPRINT",EDGE,{"disambiguationData":[TD([[subQ2,1.0]])],"derivedFrom":subQ1}),1.0]])]})]);}
            var Q1;
            {var subQ0=sQuery(id+"F5.wireOp",EDGE,"E102.left");Q1=makeQuery(id+"F5.imprint","IMPRINT",FACE,{"disambiguationData":[TD([[makeQuery(id+"F5.imprint","IMPRINT",EDGE,{"derivedFrom":subQ0}),-1.0]])]});}
            var Q2;
            {var subQ0=sQuery(id+"F5.wireOp",EDGE,"E114.right");var subQ1=sQuery(id+"F5.wireOp",EDGE,"E106.MirrorCS");var subQ2=makeQuery(id+"F5.imprint","INTERSECT",VERTEX,{"derivedFrom":[subQ1,subQ0]});var subQ3=sQuery(id+"F5.wireOp",EDGE,"E115.left");var subQ4=makeQuery(id+"F5.imprint","INTERSECT",VERTEX,{"derivedFrom":[subQ1,subQ3]});var subQ10=sQuery(id+"F5.wireOp",EDGE,"E109.MirrorCS");var subQ15=sQuery(id+"F5.wireOp",EDGE,"E115.right");var subQ16=makeQuery(id+"F5.imprint","INTERSECT",VERTEX,{"derivedFrom":[subQ1,subQ15]});var subQ23=sQuery(id+"F5.wireOp",EDGE,"E116.right");var subQ24=makeQuery(id+"F5.imprint","INTERSECT",VERTEX,{"derivedFrom":[subQ1,subQ23]});var subQ27=sQuery(id+"F5.wireOp",EDGE,"E108.MirrorCS");var subQ32=sQuery(id+"F5.wireOp",EDGE,"E117.left");var subQ33=makeQuery(id+"F5.imprint","INTERSECT",VERTEX,{"derivedFrom":[subQ1,subQ32]});Q2=qUnion([makeQuery(id+"F5.imprint","IMPRINT",FACE,{"disambiguationData":[TD([[makeQuery(id+"F5.imprint","IMPRINT",EDGE,{"disambiguationData":[TD([[subQ33,1.0]])],"derivedFrom":subQ1}),-1.0]])]}),makeQuery(id+"F5.imprint","IMPRINT",FACE,{"disambiguationData":[TD([[makeQuery(id+"F5.imprint","IMPRINT",EDGE,{"disambiguationData":[TD([[subQ33,-1.0]])],"derivedFrom":subQ1}),-1.0]])]}),makeQuery(id+"F5.imprint","IMPRINT",FACE,{"disambiguationData":[TD([[makeQuery(id+"F5.imprint","IMPRINT",EDGE,{"disambiguationData":[TD([[subQ4,1.0]])],"derivedFrom":subQ1}),-1.0]])]}),makeQuery(id+"F5.imprint","IMPRINT",FACE,{"disambiguationData":[TD([[makeQuery(id+"F5.imprint","IMPRINT",EDGE,{"derivedFrom":subQ27}),1.0]])]}),makeQuery(id+"F5.imprint","IMPRINT",FACE,{"disambiguationData":[TD([[makeQuery(id+"F5.imprint","IMPRINT",EDGE,{"disambiguationData":[TD([[subQ24,-1.0]])],"derivedFrom":subQ1}),-1.0]])]}),makeQuery(id+"F5.imprint","IMPRINT",FACE,{"disambiguationData":[TD([[makeQuery(id+"F5.imprint","IMPRINT",EDGE,{"disambiguationData":[TD([[subQ2,-1.0]])],"derivedFrom":subQ1}),-1.0]])]}),makeQuery(id+"F5.imprint","IMPRINT",FACE,{"disambiguationData":[TD([[makeQuery(id+"F5.imprint","IMPRINT",EDGE,{"disambiguationData":[TD([[subQ16,1.0]])],"derivedFrom":subQ1}),-1.0]])]}),makeQuery(id+"F5.imprint","IMPRINT",FACE,{"disambiguationData":[TD([[makeQuery(id+"F5.imprint","IMPRINT",EDGE,{"derivedFrom":subQ10}),-1.0]])]}),makeQuery(id+"F5.imprint","IMPRINT",FACE,{"disambiguationData":[TD([[makeQuery(id+"F5.imprint","IMPRINT",EDGE,{"disambiguationData":[TD([[subQ2,1.0]])],"derivedFrom":subQ1}),-1.0]])]})]);}
            var Q3;
            {var subQ0=sQuery(id+"F5.wireOp",EDGE,"E102.right");Q3=makeQuery(id+"F5.imprint","IMPRINT",FACE,{"disambiguationData":[TD([[makeQuery(id+"F5.imprint","IMPRINT",EDGE,{"derivedFrom":subQ0}),1.0]])]});}
            var Q4;
            {var subQ0=sQuery(id+"F5.wireOp",EDGE,"E115.left");var subQ1=sQuery(id+"F5.wireOp",EDGE,"E102.bottom");var subQ2=makeQuery(id+"F5.imprint","INTERSECT",VERTEX,{"derivedFrom":[subQ1,subQ0]});Q4=makeQuery(id+"F5.imprint","IMPRINT",FACE,{"disambiguationData":[TD([[makeQuery(id+"F5.imprint","IMPRINT",EDGE,{"disambiguationData":[TD([[subQ2,-1.0]])],"derivedFrom":subQ1}),1.0]])]});}
            var Q5;
            {var subQ0=sQuery(id+"F5.wireOp",EDGE,"E114.right");var subQ1=sQuery(id+"F5.wireOp",EDGE,"E102.bottom");var subQ2=makeQuery(id+"F5.imprint","INTERSECT",VERTEX,{"derivedFrom":[subQ1,subQ0]});Q5=makeQuery(id+"F5.imprint","IMPRINT",FACE,{"disambiguationData":[TD([[makeQuery(id+"F5.imprint","IMPRINT",EDGE,{"disambiguationData":[TD([[subQ2,-1.0]])],"derivedFrom":subQ1}),1.0]])]});}
            var Q6;
            {var subQ0=sQuery(id+"F5.wireOp",EDGE,"E102.right");Q6=makeQuery(id+"F5.imprint","IMPRINT",FACE,{"disambiguationData":[TD([[makeQuery(id+"F5.imprint","IMPRINT",EDGE,{"derivedFrom":subQ0}),1.0]])]});}
            var Q7;
            {var subQ0=sQuery(id+"F5.wireOp",EDGE,"E115.left");var subQ1=sQuery(id+"F5.wireOp",EDGE,"E102.bottom");var subQ2=makeQuery(id+"F5.imprint","INTERSECT",VERTEX,{"derivedFrom":[subQ1,subQ0]});Q7=makeQuery(id+"F5.imprint","IMPRINT",FACE,{"disambiguationData":[TD([[makeQuery(id+"F5.imprint","IMPRINT",EDGE,{"disambiguationData":[TD([[subQ2,1.0]])],"derivedFrom":subQ1}),1.0]])]});}
            var Q8;
            {var subQ0=sQuery(id+"F5.wireOp",EDGE,"E116.left");var subQ1=sQuery(id+"F5.wireOp",EDGE,"E102.bottom");var subQ2=makeQuery(id+"F5.imprint","INTERSECT",VERTEX,{"derivedFrom":[subQ1,subQ0]});Q8=makeQuery(id+"F5.imprint","IMPRINT",FACE,{"disambiguationData":[TD([[makeQuery(id+"F5.imprint","IMPRINT",EDGE,{"disambiguationData":[TD([[subQ2,-1.0]])],"derivedFrom":subQ1}),1.0]])]});}
            var Q9;
            {var subQ0=sQuery(id+"F5.wireOp",EDGE,"E116.left");var subQ1=sQuery(id+"F5.wireOp",EDGE,"E102.bottom");var subQ2=makeQuery(id+"F5.imprint","INTERSECT",VERTEX,{"derivedFrom":[subQ1,subQ0]});Q9=makeQuery(id+"F5.imprint","IMPRINT",FACE,{"disambiguationData":[TD([[makeQuery(id+"F5.imprint","IMPRINT",EDGE,{"disambiguationData":[TD([[subQ2,1.0]])],"derivedFrom":subQ1}),1.0]])]});}
            var Q10;
            {var subQ0=sQuery(id+"F5.wireOp",EDGE,"E117.left");var subQ1=sQuery(id+"F5.wireOp",EDGE,"E102.bottom");var subQ2=makeQuery(id+"F5.imprint","INTERSECT",VERTEX,{"derivedFrom":[subQ1,subQ0]});Q10=makeQuery(id+"F5.imprint","IMPRINT",FACE,{"disambiguationData":[TD([[makeQuery(id+"F5.imprint","IMPRINT",EDGE,{"disambiguationData":[TD([[subQ2,-1.0]])],"derivedFrom":subQ1}),1.0]])]});}
            var Q11;
            {var subQ0=sQuery(id+"F5.wireOp",EDGE,"E117.left");var subQ1=sQuery(id+"F5.wireOp",EDGE,"E102.bottom");var subQ2=makeQuery(id+"F5.imprint","INTERSECT",VERTEX,{"derivedFrom":[subQ1,subQ0]});Q11=makeQuery(id+"F5.imprint","IMPRINT",FACE,{"disambiguationData":[TD([[makeQuery(id+"F5.imprint","IMPRINT",EDGE,{"disambiguationData":[TD([[subQ2,1.0]])],"derivedFrom":subQ1}),1.0]])]});}
            extrude(context, id + "F6", {"entities" : qUnion([Q0, Q1, Q2, Q3, Q4, Q5, Q6, Q7, Q8, Q9, Q10, Q11]), "operationType" : NewBodyOperationType.REMOVE, "oppositeDirection" : true, "depth" : 5.84 * mm, "offsetDistance" : 25.4 * mm});
        }
        {
            var Q0;
            Q0=makeQuery(id+"F5.imprint","IMPRINT",FACE,{"disambiguationData":[TD([[makeQuery(id+"F5.imprint","IMPRINT",EDGE,{"derivedFrom":sQuery(id+"F5.wireOp",EDGE,"E82.0")}),1.0]])]});
            extrude(context, id + "F7", {"entities" : qUnion([Q0]), "operationType" : NewBodyOperationType.REMOVE, "oppositeDirection" : true, "depth" : 6.35 * mm, "offsetDistance" : 25.4 * mm});
        }
        {
            var Q0;
            {var subQ0=sQuery(id+"F5.wireOp",EDGE,"E114.left");var subQ1=sQuery(id+"F5.wireOp",EDGE,"E90.trimOffspring");var subQ2=makeQuery(id+"F5.imprint","INTERSECT",VERTEX,{"derivedFrom":[subQ1,subQ0]});Q0=makeQuery(id+"F5.imprint","IMPRINT",FACE,{"disambiguationData":[TD([[makeQuery(id+"F5.imprint","IMPRINT",EDGE,{"disambiguationData":[TD([[subQ2,1.0]])],"derivedFrom":subQ1}),-1.0]])]});}
            var Q1;
            {var subQ0=sQuery(id+"F5.wireOp",EDGE,"E114.left");var subQ1=sQuery(id+"F5.wireOp",EDGE,"E102.top");var subQ2=makeQuery(id+"F5.imprint","INTERSECT",VERTEX,{"derivedFrom":[subQ1,subQ0]});Q1=makeQuery(id+"F5.imprint","IMPRINT",FACE,{"disambiguationData":[TD([[makeQuery(id+"F5.imprint","IMPRINT",EDGE,{"disambiguationData":[TD([[subQ2,1.0]])],"derivedFrom":subQ1}),1.0]])]});}
            var Q2;
            {var subQ0=sQuery(id+"F5.wireOp",EDGE,"E114.right");var subQ1=sQuery(id+"F5.wireOp",EDGE,"E102.bottom");var subQ2=makeQuery(id+"F5.imprint","INTERSECT",VERTEX,{"derivedFrom":[subQ1,subQ0]});Q2=makeQuery(id+"F5.imprint","IMPRINT",FACE,{"disambiguationData":[TD([[makeQuery(id+"F5.imprint","IMPRINT",EDGE,{"disambiguationData":[TD([[subQ2,-1.0]])],"derivedFrom":subQ1}),-1.0]])]});}
            var Q3;
            {var subQ0=sQuery(id+"F5.wireOp",EDGE,"E114.left");var subQ1=sQuery(id+"F5.wireOp",EDGE,"E100.trimOffspring");var subQ2=makeQuery(id+"F5.imprint","INTERSECT",VERTEX,{"derivedFrom":[subQ1,subQ0]});Q3=makeQuery(id+"F5.imprint","IMPRINT",FACE,{"disambiguationData":[TD([[makeQuery(id+"F5.imprint","IMPRINT",EDGE,{"disambiguationData":[TD([[subQ2,1.0]])],"derivedFrom":subQ1}),1.0]])]});}
            var Q4;
            {var subQ0=sQuery(id+"F5.wireOp",EDGE,"E115.left");var subQ1=sQuery(id+"F5.wireOp",EDGE,"E102.top");var subQ2=makeQuery(id+"F5.imprint","INTERSECT",VERTEX,{"derivedFrom":[subQ1,subQ0]});Q4=makeQuery(id+"F5.imprint","IMPRINT",FACE,{"disambiguationData":[TD([[makeQuery(id+"F5.imprint","IMPRINT",EDGE,{"disambiguationData":[TD([[subQ2,1.0]])],"derivedFrom":subQ1}),1.0]])]});}
            var Q5;
            {var subQ0=sQuery(id+"F5.wireOp",EDGE,"E115.left");var subQ1=sQuery(id+"F5.wireOp",EDGE,"E90.trimOffspring");var subQ2=makeQuery(id+"F5.imprint","INTERSECT",VERTEX,{"derivedFrom":[subQ1,subQ0]});Q5=makeQuery(id+"F5.imprint","IMPRINT",FACE,{"disambiguationData":[TD([[makeQuery(id+"F5.imprint","IMPRINT",EDGE,{"disambiguationData":[TD([[subQ2,1.0]])],"derivedFrom":subQ1}),-1.0]])]});}
            var Q6;
            {var subQ0=sQuery(id+"F5.wireOp",EDGE,"E115.left");var subQ1=sQuery(id+"F5.wireOp",EDGE,"E102.bottom");var subQ2=makeQuery(id+"F5.imprint","INTERSECT",VERTEX,{"derivedFrom":[subQ1,subQ0]});Q6=makeQuery(id+"F5.imprint","IMPRINT",FACE,{"disambiguationData":[TD([[makeQuery(id+"F5.imprint","IMPRINT",EDGE,{"disambiguationData":[TD([[subQ2,1.0]])],"derivedFrom":subQ1}),-1.0]])]});}
            var Q7;
            {var subQ0=sQuery(id+"F5.wireOp",EDGE,"E115.left");var subQ1=sQuery(id+"F5.wireOp",EDGE,"E100.trimOffspring");var subQ2=makeQuery(id+"F5.imprint","INTERSECT",VERTEX,{"derivedFrom":[subQ1,subQ0]});Q7=makeQuery(id+"F5.imprint","IMPRINT",FACE,{"disambiguationData":[TD([[makeQuery(id+"F5.imprint","IMPRINT",EDGE,{"disambiguationData":[TD([[subQ2,1.0]])],"derivedFrom":subQ1}),1.0]])]});}
            var Q8;
            {var subQ0=sQuery(id+"F5.wireOp",EDGE,"E116.left");var subQ1=sQuery(id+"F5.wireOp",EDGE,"E100.trimOffspring");var subQ2=makeQuery(id+"F5.imprint","INTERSECT",VERTEX,{"derivedFrom":[subQ1,subQ0]});Q8=makeQuery(id+"F5.imprint","IMPRINT",FACE,{"disambiguationData":[TD([[makeQuery(id+"F5.imprint","IMPRINT",EDGE,{"disambiguationData":[TD([[subQ2,1.0]])],"derivedFrom":subQ1}),1.0]])]});}
            var Q9;
            {var subQ0=sQuery(id+"F5.wireOp",EDGE,"E116.left");var subQ1=sQuery(id+"F5.wireOp",EDGE,"E102.bottom");var subQ2=makeQuery(id+"F5.imprint","INTERSECT",VERTEX,{"derivedFrom":[subQ1,subQ0]});Q9=makeQuery(id+"F5.imprint","IMPRINT",FACE,{"disambiguationData":[TD([[makeQuery(id+"F5.imprint","IMPRINT",EDGE,{"disambiguationData":[TD([[subQ2,1.0]])],"derivedFrom":subQ1}),-1.0]])]});}
            var Q10;
            {var subQ0=sQuery(id+"F5.wireOp",EDGE,"E116.left");var subQ1=sQuery(id+"F5.wireOp",EDGE,"E102.top");var subQ2=makeQuery(id+"F5.imprint","INTERSECT",VERTEX,{"derivedFrom":[subQ1,subQ0]});Q10=makeQuery(id+"F5.imprint","IMPRINT",FACE,{"disambiguationData":[TD([[makeQuery(id+"F5.imprint","IMPRINT",EDGE,{"disambiguationData":[TD([[subQ2,1.0]])],"derivedFrom":subQ1}),1.0]])]});}
            var Q11;
            {var subQ0=sQuery(id+"F5.wireOp",EDGE,"E116.right");var subQ1=sQuery(id+"F5.wireOp",EDGE,"E90.trimOffspring");var subQ2=makeQuery(id+"F5.imprint","INTERSECT",VERTEX,{"derivedFrom":[subQ1,subQ0]});Q11=makeQuery(id+"F5.imprint","IMPRINT",FACE,{"disambiguationData":[TD([[makeQuery(id+"F5.imprint","IMPRINT",EDGE,{"disambiguationData":[TD([[subQ2,-1.0]])],"derivedFrom":subQ1}),-1.0]])]});}
            var Q12;
            {var subQ0=sQuery(id+"F5.wireOp",EDGE,"E117.left");var subQ1=sQuery(id+"F5.wireOp",EDGE,"E90.trimOffspring");var subQ2=makeQuery(id+"F5.imprint","INTERSECT",VERTEX,{"derivedFrom":[subQ1,subQ0]});Q12=makeQuery(id+"F5.imprint","IMPRINT",FACE,{"disambiguationData":[TD([[makeQuery(id+"F5.imprint","IMPRINT",EDGE,{"disambiguationData":[TD([[subQ2,1.0]])],"derivedFrom":subQ1}),-1.0]])]});}
            var Q13;
            {var subQ0=sQuery(id+"F5.wireOp",EDGE,"E117.left");var subQ1=sQuery(id+"F5.wireOp",EDGE,"E102.top");var subQ2=makeQuery(id+"F5.imprint","INTERSECT",VERTEX,{"derivedFrom":[subQ1,subQ0]});Q13=makeQuery(id+"F5.imprint","IMPRINT",FACE,{"disambiguationData":[TD([[makeQuery(id+"F5.imprint","IMPRINT",EDGE,{"disambiguationData":[TD([[subQ2,1.0]])],"derivedFrom":subQ1}),1.0]])]});}
            var Q14;
            {var subQ0=sQuery(id+"F5.wireOp",EDGE,"E117.left");var subQ1=sQuery(id+"F5.wireOp",EDGE,"E102.bottom");var subQ2=makeQuery(id+"F5.imprint","INTERSECT",VERTEX,{"derivedFrom":[subQ1,subQ0]});Q14=makeQuery(id+"F5.imprint","IMPRINT",FACE,{"disambiguationData":[TD([[makeQuery(id+"F5.imprint","IMPRINT",EDGE,{"disambiguationData":[TD([[subQ2,1.0]])],"derivedFrom":subQ1}),-1.0]])]});}
            var Q15;
            {var subQ0=sQuery(id+"F5.wireOp",EDGE,"E117.right");var subQ1=sQuery(id+"F5.wireOp",EDGE,"E100.trimOffspring");var subQ2=makeQuery(id+"F5.imprint","INTERSECT",VERTEX,{"derivedFrom":[subQ1,subQ0]});Q15=makeQuery(id+"F5.imprint","IMPRINT",FACE,{"disambiguationData":[TD([[makeQuery(id+"F5.imprint","IMPRINT",EDGE,{"disambiguationData":[TD([[subQ2,-1.0]])],"derivedFrom":subQ1}),1.0]])]});}
            extrude(context, id + "F8", {"entities" : qUnion([Q0, Q1, Q2, Q3, Q4, Q5, Q6, Q7, Q8, Q9, Q10, Q11, Q12, Q13, Q14, Q15]), "operationType" : NewBodyOperationType.REMOVE, "oppositeDirection" : true, "depth" : 3.17 * mm, "offsetDistance" : 25.4 * mm});
        }
        {
            var Q0;
            Q0=makeQuery(id+"F3.imprint","IMPRINT",FACE,{"disambiguationData":[TD([[makeQuery(id+"F3.imprint","IMPRINT",EDGE,{"derivedFrom":sQuery(id+"F3.wireOp",EDGE,"E53")}),1.0]])]});
            extrude(context, id + "F9", {"entities" : qUnion([Q0]), "operationType" : NewBodyOperationType.REMOVE, "endBound" : BoundingType.THROUGH_ALL, "oppositeDirection" : true, "depth" : 25.4 * mm, "offsetDistance" : 25.4 * mm});
        }
        {
            var Q0;
            Q0=makeQuery(id+"F3.imprint","IMPRINT",FACE,{"disambiguationData":[TD([[makeQuery(id+"F3.imprint","IMPRINT",EDGE,{"derivedFrom":sQuery(id+"F3.wireOp",EDGE,"E53")}),-1.0]])]});
            extrude(context, id + "F10", {"entities" : qUnion([Q0]), "operationType" : NewBodyOperationType.REMOVE, "oppositeDirection" : true, "depth" : 12.7 * mm, "offsetDistance" : 25.4 * mm});
        }
        {
            var Q0;
            {var subQ3=sQuery(id+"F0.wireOp",EDGE,"E12.MirrorCS");var subQ7=sQuery(id+"F0.wireOp",EDGE,"E6.MirrorCS");Q0=makeQuery(id+"F7.boolean.opBoolean","SPLIT",FACE,{"disambiguationData":[TD([makeQuery(id+"F1.opExtrude","SWEPT_FACE",FACE,{"disambiguationData":[OSD([subQ3])]})])],"derivedFrom":makeQuery(id+"F1.opExtrude","SWEPT_FACE",FACE,{"disambiguationData":[OSD([subQ7])]})});}
            var sketch = newSketch(context, id + "F11", { "sketchPlane" : qUnion([Q0])});
            skLineSegment(sketch, "E118", {"start": v(49.88, -57.5) * mm, "end": v(-125.12, -57.5) * mm, "construction": true});
            skLineSegment(sketch, "E119", {"start": v(-37.62, 0) * mm, "end": v(-37.62, -115) * mm, "construction": true});
            skLineSegment(sketch, "E120.0", {"start": v(9.45, -100.65) * mm, "end": v(9.45, -14.35) * mm, "construction": true});
            skLineSegment(sketch, "E121.0", {"start": v(3.1, -100.65) * mm, "end": v(3.1, -14.35) * mm, "construction": true});
            skLineSegment(sketch, "E122.bottom", {"start": v(9.45, -14.35) * mm, "end": v(3.1, -14.35) * mm, "construction": true});
            skLineSegment(sketch, "E122.top", {"start": v(9.45, -100.65) * mm, "end": v(3.1, -100.65) * mm, "construction": true});
            skLineSegment(sketch, "E122.left", {"start": v(9.45, -14.35) * mm, "end": v(9.45, -100.65) * mm, "construction": true});
            skLineSegment(sketch, "E122.right", {"start": v(3.1, -14.35) * mm, "end": v(3.1, -100.65) * mm, "construction": true});
            skLineSegment(sketch, "E123", {"start": v(9.45, -37.36) * mm, "end": v(3.1, -37.36) * mm, "construction": true});
            skLineSegment(sketch, "E124", {"start": v(9.45, -31) * mm, "end": v(3.1, -31) * mm, "construction": true});
            skLineSegment(sketch, "E125", {"start": v(6.27, -31) * mm, "end": v(6.27, -37.36) * mm, "construction": true});
            skLineSegment(sketch, "E126", {"start": v(9.45, -37.36) * mm, "end": v(9.45, -31) * mm, "construction": true});
            skLineSegment(sketch, "E127", {"start": v(9.45, -34.18) * mm, "end": v(3.1, -34.18) * mm, "construction": true});
            skCircle(sketch, "E128", {"center": v(6.27, -34.18) * mm, "radius": 3.81 * mm});
            skCircle(sketch, "E129.MirrorC", {"center": v(6.27, -80.82) * mm, "radius": 3.81 * mm});
            skSolve(sketch);
        }
        {
            var Q0;
            Q0=makeQuery(id+"F11.imprint","IMPRINT",FACE,{"disambiguationData":[TD([[makeQuery(id+"F11.imprint","IMPRINT",EDGE,{"derivedFrom":sQuery(id+"F11.wireOp",EDGE,"E128")}),1.0]])]});
            var Q1;
            Q1=makeQuery(id+"F11.imprint","IMPRINT",FACE,{"disambiguationData":[TD([[makeQuery(id+"F11.imprint","IMPRINT",EDGE,{"derivedFrom":sQuery(id+"F11.wireOp",EDGE,"E129.MirrorC")}),-1.0]])]});
            extrude(context, id + "F12", {"entities" : qUnion([Q0, Q1]), "operationType" : NewBodyOperationType.REMOVE, "oppositeDirection" : true, "depth" : 25.4 * mm, "offsetDistance" : 25.4 * mm});
        }
    });
